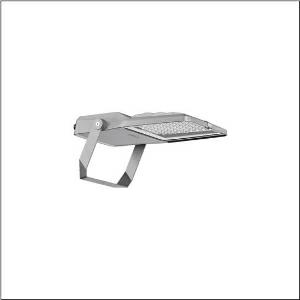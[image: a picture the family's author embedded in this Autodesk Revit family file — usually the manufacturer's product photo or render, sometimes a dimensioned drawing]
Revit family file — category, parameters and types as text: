
# Revit family: floodlight_fl_21_iq_mini___pl61_5xa7771d2c1a_1090
name_source: partatom
category: Lighting Fixtures
units: mm (PartAtom-declared; Revit-internal decimal feet)

## family parameters
Cut with Voids When Loaded = No
Host = Face
Light Source = No
Part Type = Normal
Room Calculation Point = No
Round Connector Dimension = Use Diameter
Shared = No

## types (1)
- --- (1 x LED, 17500 lm, 143 W, 3000K)
    Apparent Load = 143 VA
    CIE Flux Codes = 33 65 98 100 100
    Color Rendering = 70
    Color Temperature = 3000K
    Default Elevation = 1800 mm
    Description = Floodlight FL 21 iQ mini, floodlight, primary light control with lens, of PMMA, primary optical cover: protective disc, of toughened safety glass, transparent, light distribution: PL61, light emission: direct distribution, installation type: surface-mounted, LED, High Power LED, rated luminous flux: 17.500lm, luminous efficacy: 122lm/W, light colour: 730, colour temperature: 3000K, control gear: iQ Comfort/DALI, control: Auto-Match, Temp-Guard, Lumen-Switch, Night-Set, Smart-Wire, Light-Fading, Desk-Remote (wireless, voltage-free reading and setting of iQ features in the workshop via application-optimized NFC function/RFID function), optimised constant luminous flux control (CLO 2.0), with terminal, 6-pole, mains connection: 220..240V, AC, 50/60Hz, start of lifetime: 143W, end of service life: 152W, reduction: 61W, luminaire housing, of diecast aluminium, powder-coated, Siteco® metallic grey (DB 702S), corrosivity category C5 mid according to DIN EN ISO 12944, suitable for swimming pools, chlorine-resistant, sealing non-destructively replaceable, mounting bracket, of steel, galvanised, powder-coated, Siteco® metallic grey (DB 702S), protection rating (complete): IP66, insulation class (complete): insulation class II (safety insulation), certification: CE, ENEC, VDE, protection symbol: D, impact resistance: IK08, permissible operating ambient temperature: -40..+40°C, permissible operating ambient temperature for outdoor applications: -40..+50°C, standard: DIN EN 12944, LABS conformity tested according to VDMA 24364:2018-05, packaging unit: 1 piece

Light Distribution: PL61
    Height = 70 mm
    Lamp = 1 x LED
    Lamp Light Flux = 17500 lm
    Lamp Power = 143 W
    Lamp count = 1
    Length = 485 mm
    Luminous efficacy = 122 lm/W
    Manufacturer = Siteco
    ModVariant = No
    Model = 5XA7771D2C1A
    Number of Poles = 1
    OnlyDefault = Yes
    Power Factor = 1
    Product Name = Floodlight FL 21 iQ mini | PL61
    Product group = floodlight | pylon annexe
    ProductGroupID = 6200
    Protection Class = Protection class II
    Protection Degree = IP 66
    RLX_Detail_Level = 1
    RLX_Emergency_Light_Flux = 0 lm
    RLX_Emergency_Type = 0
    RLX_Emergency_Type_DB = No
    RlxData = <blob elided: 96709 chars, md5=8623ba23>
    Socket = socket
    Standby Power = 0 W
    System Light Flux = 17500 lm
    System Power = 143 W
    Type Comments = factory setting: luminous flux: 100 % | dim-lin: 254 | 730 mA
    Type Image = l_1006845.jpg
    URL = http://relux.com
    VarID = @adj_172794
    Voltage = 0 V
    Weight = 0.00 kg
    Width = 337 mm

## geometry (parser evidence)
native form markers: Blend x4, Sweep x11
no freeform markers — native parametric forms only
